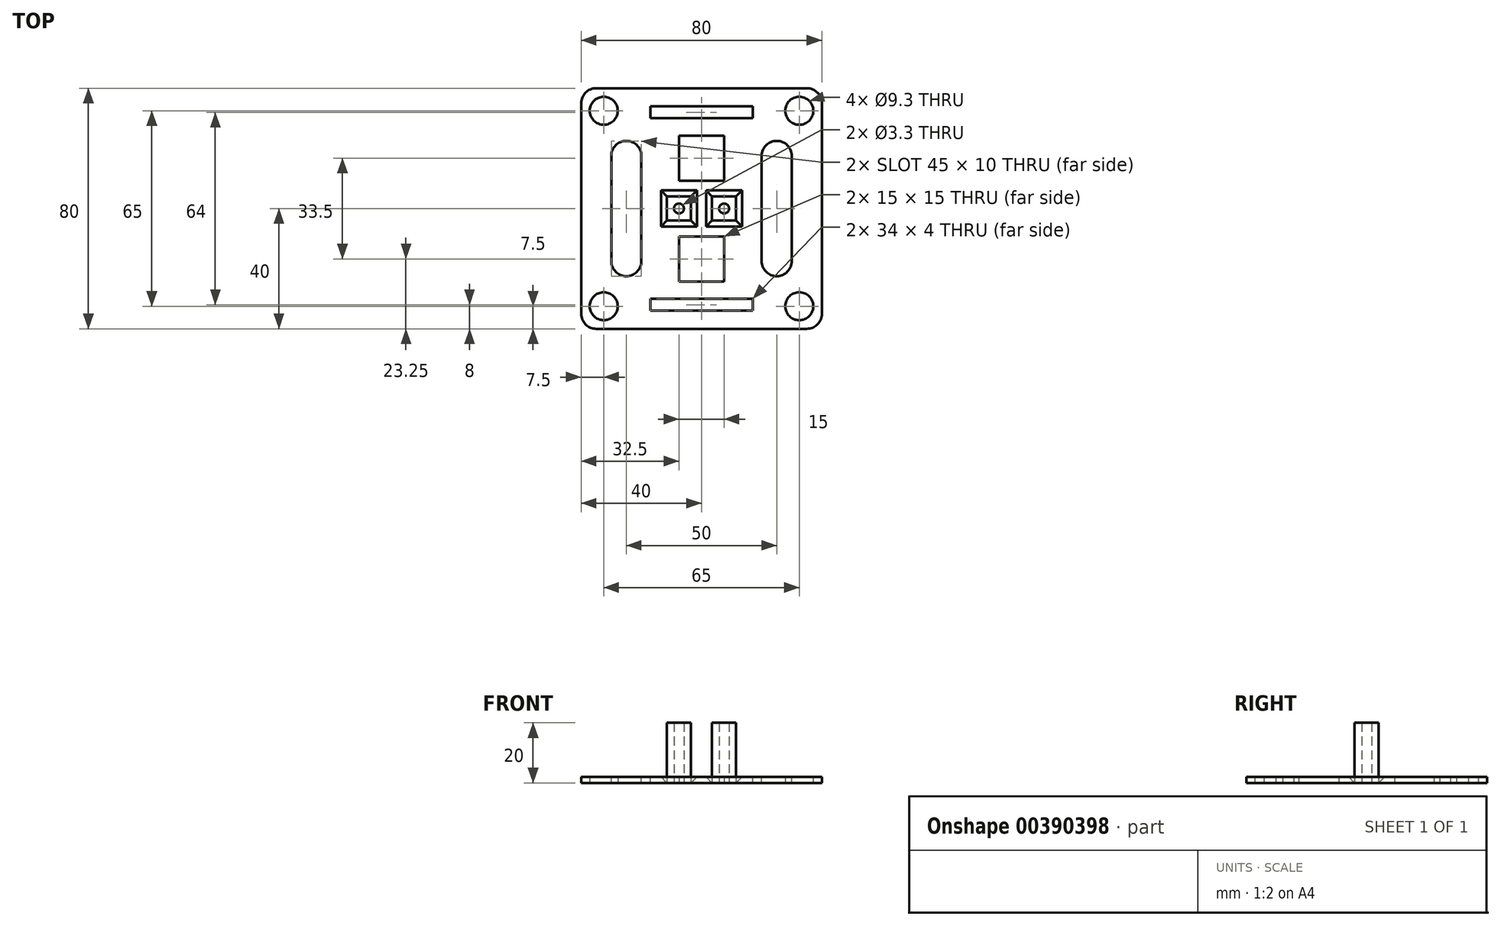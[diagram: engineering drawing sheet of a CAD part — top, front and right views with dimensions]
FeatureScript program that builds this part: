
annotation { "Feature Type Name" : "Feature", "Feature Type Description" : "" }
export const myFeature = defineFeature(function(context is Context, id is Id, definition is map)
    precondition{}
    {
        {
            var Q0;
            Q0=qCreatedBy(makeId("Top.planeOp"),FACE);
            var sketch = newSketch(context, id + "F0", { "sketchPlane" : qUnion([Q0])});
            skLineSegment(sketch, "E0.bottom", {"start": v(0, 0) * mm, "end": v(80, 0) * mm});
            skLineSegment(sketch, "E0.top", {"start": v(0, 80) * mm, "end": v(80, 80) * mm});
            skLineSegment(sketch, "E0.left", {"start": v(0, 0) * mm, "end": v(0, 80) * mm});
            skLineSegment(sketch, "E0.right", {"start": v(80, 0) * mm, "end": v(80, 80) * mm});
            skLineSegment(sketch, "E1", {"start": v(40, 80) * mm, "end": v(40, 0) * mm, "construction": true});
            skLineSegment(sketch, "E2", {"start": v(80, 40) * mm, "end": v(0, 40) * mm, "construction": true});
            skCircle(sketch, "E3", {"center": v(40, 40) * mm, "radius": 7.5 * mm, "construction": true});
            skCircle(sketch, "E4", {"center": v(47.5, 40) * mm, "radius": 1.65 * mm});
            skCircle(sketch, "E5", {"center": v(32.5, 40) * mm, "radius": 1.65 * mm});
            skLineSegment(sketch, "E6", {"start": v(47.5, 80) * mm, "end": v(47.5, 0) * mm, "construction": true});
            skLineSegment(sketch, "E7", {"start": v(32.5, 80) * mm, "end": v(32.5, 0) * mm, "construction": true});
            skLineSegment(sketch, "E8.bottom", {"start": v(28.5, 44) * mm, "end": v(36.5, 44) * mm});
            skLineSegment(sketch, "E8.top", {"start": v(28.5, 36) * mm, "end": v(36.5, 36) * mm});
            skLineSegment(sketch, "E8.left", {"start": v(28.5, 44) * mm, "end": v(28.5, 36) * mm});
            skLineSegment(sketch, "E8.right", {"start": v(36.5, 44) * mm, "end": v(36.5, 36) * mm});
            skLineSegment(sketch, "E9.bottom", {"start": v(43.5, 44) * mm, "end": v(51.5, 44) * mm});
            skLineSegment(sketch, "E9.top", {"start": v(43.5, 36) * mm, "end": v(51.5, 36) * mm});
            skLineSegment(sketch, "E9.left", {"start": v(43.5, 44) * mm, "end": v(43.5, 36) * mm});
            skLineSegment(sketch, "E9.right", {"start": v(51.5, 44) * mm, "end": v(51.5, 36) * mm});
            skLineSegment(sketch, "E10", {"start": v(80, 80) * mm, "end": v(0, 0) * mm, "construction": true});
            skLineSegment(sketch, "E11", {"start": v(0, 80) * mm, "end": v(80, 0) * mm, "construction": true});
            skLineSegment(sketch, "E12.bottom", {"start": v(7.5, 72.5) * mm, "end": v(72.5, 72.5) * mm, "construction": true});
            skLineSegment(sketch, "E12.top", {"start": v(7.5, 7.5) * mm, "end": v(72.5, 7.5) * mm, "construction": true});
            skLineSegment(sketch, "E12.left", {"start": v(7.5, 72.5) * mm, "end": v(7.5, 7.5) * mm, "construction": true});
            skLineSegment(sketch, "E12.right", {"start": v(72.5, 72.5) * mm, "end": v(72.5, 7.5) * mm, "construction": true});
            skLineSegment(sketch, "E13.bottom", {"start": v(23.25, 56.75) * mm, "end": v(56.75, 56.75) * mm, "construction": true});
            skLineSegment(sketch, "E13.top", {"start": v(23.25, 23.25) * mm, "end": v(56.75, 23.25) * mm, "construction": true});
            skLineSegment(sketch, "E13.left", {"start": v(23.25, 56.75) * mm, "end": v(23.25, 23.25) * mm, "construction": true});
            skLineSegment(sketch, "E13.right", {"start": v(56.75, 56.75) * mm, "end": v(56.75, 23.25) * mm, "construction": true});
            skLineSegment(sketch, "E14.bottom", {"start": v(32.5, 30.75) * mm, "end": v(47.5, 30.75) * mm});
            skLineSegment(sketch, "E14.top", {"start": v(32.5, 15.75) * mm, "end": v(47.5, 15.75) * mm});
            skLineSegment(sketch, "E14.left", {"start": v(32.5, 30.75) * mm, "end": v(32.5, 15.75) * mm});
            skLineSegment(sketch, "E14.right", {"start": v(47.5, 30.75) * mm, "end": v(47.5, 15.75) * mm});
            skLineSegment(sketch, "E15.bottom", {"start": v(32.5, 64.25) * mm, "end": v(47.5, 64.25) * mm});
            skLineSegment(sketch, "E15.top", {"start": v(32.5, 49.25) * mm, "end": v(47.5, 49.25) * mm});
            skLineSegment(sketch, "E15.left", {"start": v(32.5, 64.25) * mm, "end": v(32.5, 49.25) * mm});
            skLineSegment(sketch, "E15.right", {"start": v(47.5, 64.25) * mm, "end": v(47.5, 49.25) * mm});
            skCircle(sketch, "E16", {"center": v(7.5, 72.5) * mm, "radius": 4.65 * mm});
            skCircle(sketch, "E17", {"center": v(7.5, 7.5) * mm, "radius": 4.65 * mm});
            skCircle(sketch, "E18", {"center": v(72.5, 7.5) * mm, "radius": 4.65 * mm});
            skCircle(sketch, "E19", {"center": v(72.5, 72.5) * mm, "radius": 4.65 * mm});
            skSolve(sketch);
        }
        {
            var Q0;
            Q0=makeQuery(id+"F0.imprint","IMPRINT",FACE,{"disambiguationData":[TD([[makeQuery(id+"F0.imprint","IMPRINT",EDGE,{"derivedFrom":sQuery(id+"F0.wireOp",EDGE,"E5")}),-1.0]])]});
            var Q1;
            Q1=makeQuery(id+"F0.imprint","IMPRINT",FACE,{"disambiguationData":[TD([[makeQuery(id+"F0.imprint","IMPRINT",EDGE,{"derivedFrom":sQuery(id+"F0.wireOp",EDGE,"E4")}),-1.0]])]});
            extrude(context, id + "F1", {"entities" : qUnion([Q0, Q1]), "depth" : 20 * mm});
        }
        {
            var Q0;
            Q0=makeQuery(id+"F0.imprint","IMPRINT",FACE,{"disambiguationData":[TD([[makeQuery(id+"F0.imprint","IMPRINT",EDGE,{"derivedFrom":sQuery(id+"F0.wireOp",EDGE,"E0.bottom")}),1.0]])]});
            extrude(context, id + "F2", {"entities" : qUnion([Q0]), "depth" : 2 * mm});
        }
        {
            var Q0;
            Q0=makeQuery(id+"F2.opExtrude","SWEPT_EDGE",EDGE,{"disambiguationData":[OSD([sQuery(id+"F0.wireOp",EDGE,"E0.top"),sQuery(id+"F0.wireOp",EDGE,"E0.left")])]});
            var Q1;
            Q1=makeQuery(id+"F2.opExtrude","SWEPT_EDGE",EDGE,{"disambiguationData":[OSD([sQuery(id+"F0.wireOp",EDGE,"E0.top"),sQuery(id+"F0.wireOp",EDGE,"E0.right")])]});
            var Q2;
            Q2=makeQuery(id+"F2.opExtrude","SWEPT_EDGE",EDGE,{"disambiguationData":[OSD([sQuery(id+"F0.wireOp",EDGE,"E0.bottom"),sQuery(id+"F0.wireOp",EDGE,"E0.right")])]});
            var Q3;
            Q3=makeQuery(id+"F2.opExtrude","SWEPT_EDGE",EDGE,{"disambiguationData":[OSD([sQuery(id+"F0.wireOp",EDGE,"E0.bottom"),sQuery(id+"F0.wireOp",EDGE,"E0.left")])]});
            fillet(context, id + "F3", {"entities" : qUnion([Q0, Q1, Q2, Q3]), "radius" : 5 * mm, "tangentPropagation" : true, "allowEdgeOverflow" : false});
        }
        {
            var Q0;
            Q0=makeQuery(id+"F2.opExtrude","CAP_EDGE",EDGE,{"disambiguationData":[OSD([sQuery(id+"F0.wireOp",EDGE,"E8.bottom")])],"isStart":false});
            var Q1;
            Q1=makeQuery(id+"F2.opExtrude","CAP_EDGE",EDGE,{"disambiguationData":[OSD([sQuery(id+"F0.wireOp",EDGE,"E9.bottom")])],"isStart":false});
            chamfer(context, id + "F4", {"entities" : qUnion([Q0, Q1]), "width" : 2 * mm, "tangentPropagation" : true});
        }
        {
            var Q0;
            Q0=makeQuery(id+"F2.opExtrude","CAP_EDGE",EDGE,{"disambiguationData":[OSD([sQuery(id+"F0.wireOp",EDGE,"E8.top")])],"isStart":false});
            var Q1;
            Q1=makeQuery(id+"F2.opExtrude","CAP_EDGE",EDGE,{"disambiguationData":[OSD([sQuery(id+"F0.wireOp",EDGE,"E9.top")])],"isStart":false});
            chamfer(context, id + "F5", {"entities" : qUnion([Q0, Q1]), "width" : 2 * mm, "tangentPropagation" : true});
        }
        {
            var Q0;
            Q0=makeQuery(id+"F2.opExtrude","CAP_EDGE",EDGE,{"disambiguationData":[OSD([sQuery(id+"F0.wireOp",EDGE,"E8.left")])],"isStart":false});
            var Q1;
            Q1=makeQuery(id+"F2.opExtrude","CAP_EDGE",EDGE,{"disambiguationData":[OSD([sQuery(id+"F0.wireOp",EDGE,"E8.right")])],"isStart":false});
            chamfer(context, id + "F6", {"entities" : qUnion([Q0, Q1]), "width" : 2 * mm, "tangentPropagation" : true});
        }
        {
            var Q0;
            Q0=makeQuery(id+"F2.opExtrude","CAP_EDGE",EDGE,{"disambiguationData":[OSD([sQuery(id+"F0.wireOp",EDGE,"E9.right")])],"isStart":false});
            var Q1;
            Q1=makeQuery(id+"F2.opExtrude","CAP_EDGE",EDGE,{"disambiguationData":[OSD([sQuery(id+"F0.wireOp",EDGE,"E9.left")])],"isStart":false});
            chamfer(context, id + "F7", {"entities" : qUnion([Q0, Q1]), "width" : 2 * mm, "tangentPropagation" : true});
        }
        {
            var Q0;
            Q0=makeQuery(id+"F2.opExtrude","CAP_FACE",FACE,{"disambiguationData":[OSD([sQuery(id+"F0.wireOp",EDGE,"E0.bottom"),sQuery(id+"F0.wireOp",EDGE,"E0.top"),sQuery(id+"F0.wireOp",EDGE,"E0.left"),sQuery(id+"F0.wireOp",EDGE,"E0.right"),sQuery(id+"F0.wireOp",EDGE,"E8.bottom"),sQuery(id+"F0.wireOp",EDGE,"E8.top"),sQuery(id+"F0.wireOp",EDGE,"E8.left"),sQuery(id+"F0.wireOp",EDGE,"E8.right"),sQuery(id+"F0.wireOp",EDGE,"E9.bottom"),sQuery(id+"F0.wireOp",EDGE,"E9.top"),sQuery(id+"F0.wireOp",EDGE,"E9.left"),sQuery(id+"F0.wireOp",EDGE,"E9.right"),sQuery(id+"F0.wireOp",EDGE,"E14.bottom"),sQuery(id+"F0.wireOp",EDGE,"E14.top"),sQuery(id+"F0.wireOp",EDGE,"E14.left"),sQuery(id+"F0.wireOp",EDGE,"E14.right"),sQuery(id+"F0.wireOp",EDGE,"E15.bottom"),sQuery(id+"F0.wireOp",EDGE,"E15.top"),sQuery(id+"F0.wireOp",EDGE,"E15.left"),sQuery(id+"F0.wireOp",EDGE,"E15.right"),sQuery(id+"F0.wireOp",EDGE,"E16"),sQuery(id+"F0.wireOp",EDGE,"E17"),sQuery(id+"F0.wireOp",EDGE,"E18"),sQuery(id+"F0.wireOp",EDGE,"E19")])],"isStart":false});
            var sketch = newSketch(context, id + "F8", { "sketchPlane" : qUnion([Q0])});
            skLineSegment(sketch, "E20", {"start": v(56.75, 40) * mm, "end": v(80, 40) * mm, "construction": true});
            skLineSegment(sketch, "E21", {"start": v(23.25, 40) * mm, "end": v(0, 40) * mm, "construction": true});
            skLineSegment(sketch, "E22", {"start": v(40, 63.75) * mm, "end": v(40, 80) * mm, "construction": true});
            skLineSegment(sketch, "E23", {"start": v(40, 16.25) * mm, "end": v(40, 0) * mm, "construction": true});
            skLineSegment(sketch, "E24.bottom", {"start": v(65, 62.5) * mm, "end": v(65, 62.5) * mm});
            skLineSegment(sketch, "E24.top", {"start": v(65, 17.5) * mm, "end": v(65, 17.5) * mm});
            skLineSegment(sketch, "E24.left", {"start": v(60, 57.5) * mm, "end": v(60, 22.5) * mm});
            skLineSegment(sketch, "E24.right", {"start": v(70, 57.5) * mm, "end": v(70, 22.5) * mm});
            skLineSegment(sketch, "E25.bottom", {"start": v(15, 62.5) * mm, "end": v(15, 62.5) * mm});
            skLineSegment(sketch, "E25.top", {"start": v(15, 17.5) * mm, "end": v(15, 17.5) * mm});
            skLineSegment(sketch, "E25.left", {"start": v(20, 57.5) * mm, "end": v(20, 22.5) * mm});
            skLineSegment(sketch, "E25.right", {"start": v(10, 57.5) * mm, "end": v(10, 22.5) * mm});
            skPoint(sketch, "E26.visualSharp", {"position": v(10, 62.5) * mm});
            skArc(sketch, "E26.filletArc", {"start": v(15, 62.5) * mm, "mid": v(11.46, 61.04) * mm, "end": v(10, 57.5) * mm});
            skPoint(sketch, "E27.visualSharp", {"position": v(20, 62.5) * mm});
            skArc(sketch, "E27.filletArc", {"start": v(20, 57.5) * mm, "mid": v(18.54, 61.04) * mm, "end": v(15, 62.5) * mm});
            skPoint(sketch, "E28.visualSharp", {"position": v(10, 17.5) * mm});
            skArc(sketch, "E28.filletArc", {"start": v(10, 22.5) * mm, "mid": v(11.46, 18.96) * mm, "end": v(15, 17.5) * mm});
            skPoint(sketch, "E29.visualSharp", {"position": v(20, 17.5) * mm});
            skArc(sketch, "E29.filletArc", {"start": v(15, 17.5) * mm, "mid": v(18.54, 18.96) * mm, "end": v(20, 22.5) * mm});
            skPoint(sketch, "E30.visualSharp", {"position": v(60, 62.5) * mm});
            skArc(sketch, "E30.filletArc", {"start": v(65, 62.5) * mm, "mid": v(61.46, 61.04) * mm, "end": v(60, 57.5) * mm});
            skPoint(sketch, "E31.visualSharp", {"position": v(70, 62.5) * mm});
            skArc(sketch, "E31.filletArc", {"start": v(70, 57.5) * mm, "mid": v(68.54, 61.04) * mm, "end": v(65, 62.5) * mm});
            skPoint(sketch, "E32.visualSharp", {"position": v(70, 17.5) * mm});
            skArc(sketch, "E32.filletArc", {"start": v(65, 17.5) * mm, "mid": v(68.54, 18.96) * mm, "end": v(70, 22.5) * mm});
            skPoint(sketch, "E33.visualSharp", {"position": v(60, 17.5) * mm});
            skArc(sketch, "E33.filletArc", {"start": v(60, 22.5) * mm, "mid": v(61.46, 18.96) * mm, "end": v(65, 17.5) * mm});
            skLineSegment(sketch, "E34.bottom", {"start": v(23, 74) * mm, "end": v(57, 74) * mm});
            skLineSegment(sketch, "E34.top", {"start": v(23, 70) * mm, "end": v(57, 70) * mm});
            skLineSegment(sketch, "E34.left", {"start": v(23, 74) * mm, "end": v(23, 70) * mm});
            skLineSegment(sketch, "E34.right", {"start": v(57, 74) * mm, "end": v(57, 70) * mm});
            skLineSegment(sketch, "E35.bottom", {"start": v(23, 10) * mm, "end": v(57, 10) * mm});
            skLineSegment(sketch, "E35.top", {"start": v(23, 6) * mm, "end": v(57, 6) * mm});
            skLineSegment(sketch, "E35.left", {"start": v(23, 10) * mm, "end": v(23, 6) * mm});
            skLineSegment(sketch, "E35.right", {"start": v(57, 10) * mm, "end": v(57, 6) * mm});
            skSolve(sketch);
        }
        {
            var Q0;
            Q0=makeQuery(id+"F8.imprint","IMPRINT",FACE,{"disambiguationData":[TD([[makeQuery(id+"F8.imprint","IMPRINT",EDGE,{"derivedFrom":sQuery(id+"F8.wireOp",EDGE,"E25.left")}),-1.0]])]});
            var Q1;
            Q1=makeQuery(id+"F8.imprint","IMPRINT",FACE,{"disambiguationData":[TD([[makeQuery(id+"F8.imprint","IMPRINT",EDGE,{"derivedFrom":sQuery(id+"F8.wireOp",EDGE,"E24.left")}),1.0]])]});
            var Q2;
            Q2=makeQuery(id+"F8.imprint","IMPRINT",FACE,{"disambiguationData":[TD([[makeQuery(id+"F8.imprint","IMPRINT",EDGE,{"derivedFrom":sQuery(id+"F8.wireOp",EDGE,"E34.bottom")}),-1.0]])]});
            var Q3;
            Q3=makeQuery(id+"F8.imprint","IMPRINT",FACE,{"disambiguationData":[TD([[makeQuery(id+"F8.imprint","IMPRINT",EDGE,{"derivedFrom":sQuery(id+"F8.wireOp",EDGE,"E35.bottom")}),-1.0]])]});
            extrude(context, id + "F9", {"entities" : qUnion([Q0, Q1, Q2, Q3]), "operationType" : NewBodyOperationType.REMOVE, "oppositeDirection" : true, "depth" : 25 * mm});
        }
    });
